# Revit family: IS_Idealrain_B9457_BIM_DE
name_source: partatom
category: Plumbing Fixtures
revit_build: Autodesk Revit MEP 2016 (Build: 20161004_0715(x64)
units: mm (PartAtom-declared; Revit-internal decimal feet)

## family parameters
Always vertical = No
Cut with Voids When Loaded = No
OmniClass Number = 23.45.05.14.17
OmniClass Title = Showers
Part Type = Normal
Room Calculation Point = No
Round Connector Dimension = Use Diameter
Shared = No
Work Plane-Based = No

## types (1)
- B9457AA IDEALRAIN shower set with single function 120mm handspray
    Accessories = www.idealstandard.de\ersatzteile
    AreaUnits = millimeters
    AssetType = Fixed
    BIMObjectName = ISI_IdealStandard_ShowerMixers_Idealrain_B9457AA
    BIMobject category = Showers
    BOSUseNativeGeometries = 1
    BarCode = 3800861024361
    Brand = Ideal Standard
    Brand url = http://www.idealstandard.co.uk
    CodePerformance = 0
    Color = Chrome
    ConnectionType = Plumbing
    Cost = 0 $
    CurrencyUnit = €
    CurrentRevision = 1
    Date of publishing = 2017_11_21
    Description = B9457AA IDEALRAIN shower set with single function 120mm handspray
    DurationUnit = year
    EAN code = https://3800861024361
    Edition number = 1
    ExpectedLife = 25
    FaucetType = pillar
    Features = IDEALRAIN shower set with single function 120mm handspray
    Finish = Chrome
    IFC Classification = Sanitary Terminal
    IfcExportAs = IfcValveType
    IfcExportType = SHOWERMIXERS
    Installation instructions = http://www.idealstandard.de
    InstallationInstructions = www.idealstandard.de\produkte
    LinearUnits = millimeters
    MainColor = Chrome
    MaintenanceInformation = www.idealstandard.de\produkte
    Manufacturer name = Ideal Standard
    ManufacturerURL = www.idealstandard.com
    Material = Brass
    Material main = Brass
    Model = B9457AA
    ModelNumber = B9457AA
    ModelReference = B9457AA IDEALRAIN shower set with single function 120mm handspray
    NBS Reference Code = 35-06-81
    NBS Reference Description = Shower Heads
    Name = ShowerMixers_Idealrain_B9457AA_IdealStandard
    NettWeight = 0,576 kg
    Nominal height = 261
    Nominal width = 121
    NominalDepth = 164 mm  [stored 0.538058 ft]
    NominalHeight = 261 mm  [stored 0.856299 ft]
    NominalLength = 164 mm  [stored 0.538058 ft]
    NominalWidth = 121 mm  [stored 0.396982 ft]
    OmniClass Code = 23-31 17 00
    OmniClass Description = Showers
    Product Guid = 0c4f7e3d-9f2b-43a6-a295-36cb57f149c5
    Product SKU = B9457
    Product data url = https://bimobject.com
    Product family = IDEALRAIN
    Product group = Shower
    Product name = IDEALRAIN shower set with single function 120mm handspray
    Product url = http://www.idealstandard.de
    ProductInformation = www.idealstandard.de/produkte
    QR code = http://bimobject.com
    Shape = Sculptured
    Size = 121x164x261 mm
    Space = Internal
    SpareParts = www.idealstandard.de/ersatzteile
    Technical description = http://www.idealstandard.de
    TestPressure = 10bar
    URL = www.idealstandard.com
    Uniclass 1.4 Code = L7214
    Uniclass 1.4 Description = Showers
    Uniclass 2.0 Code = PR-35-06-81
    Uniclass 2.0 Description = Shower Heads
    Uniclass 2015 Code = Pr_40_20_87_77
    Uniclass 2015 Name = Shower head holder
    Uniclass2015Code = Pr_40_20_87_77
    Uniclass2015Title = Shower head holder
    Uniclass2015Version = Products v1.1
    Version = 1
    VolumeUnits = Litres
    Weight Net (Kg) = 0.58
    WorkingPressure = 1-5 Bar

note: [stored X ft] marks values corroborated as IEEE doubles in the binary element streams (Revit-internal decimal feet)

## geometry (parser evidence)
native form markers: Blend x4, Sweep x1
no freeform markers — native parametric forms only
